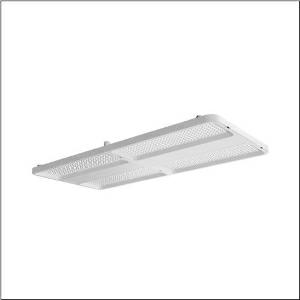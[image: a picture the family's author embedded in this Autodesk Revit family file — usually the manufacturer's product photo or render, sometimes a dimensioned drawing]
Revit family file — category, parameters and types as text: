
# Revit family: highbay_21_maxi_52hn12db4qda
name_source: partatom
category: Lighting Fixtures
units: mm (PartAtom-declared; Revit-internal decimal feet)

## family parameters
Cut with Voids When Loaded = No
Host = Face
Light Source = No
Part Type = Normal
Room Calculation Point = No
Round Connector Dimension = Use Diameter
Shared = No

## types (1)
- --- (1 x LED, 5840 lm, 31.4 W, 4000K)
    Apparent Load = 31 VA
    CIE Flux Codes = 90 98 100 100 100
    Color Rendering = 80
    Color Temperature = 4000K
    Default Elevation = 1800 mm
    Description = high bay luminaire Highbay 21 maxi; direct symmetric wide distribution, light control with lens of PMMA; UGR ≤ 22 (X = 4H | Y = 8H | S = 0.25H | reflection values 70/50/20); luminous flux: 38.000lm; light colour: 840, colour temperature: 4000K, MacAdam ≤ 3 SDCM (initial), colour rendering: CRI > 80; luminous efficacy: 192,2lm/W; rated service life: 75.000h (L80) at AT= ta max; control: DALI 2; luminaire connection: terminal, 5-pole, max. 2.5mm² (cable entry for one cable, Ø 8.5..16mm); mains connection: 230..240V, AC/DC 0/50..60Hz; connected load: 197,7W; protection rating (complete): IP66; insulation class (complete): insulation class I (protective earthing); protection symbol: D; impact resistance: IK08; certification: CE, ENEC, VDE, UKCA; luminaire for central battery installations according to EN 60598-2-22, internal wiring halogen-free; luminaire LABS conformity tested according to VDMA 24364:2018-05; Suitable for use in the food industry according to the specifications of IFS-Food, HACCP and/or BRC; housing frame of high-performance plastic PA6, matt traffic white (RAL 9016); cover of PMMA; dimension (LxWxH): 946 x 442 x 72mm; permissible operating ambient temperature: -40..+60°C (reducing of maximum allowable ambient temperature of 5°C with ceiling mounting); packaging unit: 1 piece; (delivery without accessories; please order mounting accessories separately)
    Height = 72 mm  [stored 0.23622 ft]
    Lamp = 1 x LED
    Lamp Light Flux = 5840 lm
    Lamp Power = 31.4 W
    Lamp count = 1
    Length = 946 mm
    Luminous efficacy = 186 lm/W
    Manufacturer = Siteco
    ModVariant = No
    Model = 52HN12DB4QDA
    Mounting Place = Ceiling
    Mounting Type = Pendant
    Number of Poles = 1
    OnlyDefault = Yes
    Power Factor = 1
    Product Name = Highbay 21 maxi
    Product group = high bay luminaire
    ProductGroupID = 902
    Protection Class = Protection class I
    Protection Degree = IP 66
    RLX_Detail_Level = 1
    RLX_Emergency_Light_Flux = 0 lm
    RLX_Emergency_Type = 0
    RLX_Emergency_Type_DB = No
    RlxData = <blob elided: 128149 chars, md5=0320493b>
    Socket = socket
    Standby Power = 0 W
    System Light Flux = 5840 lm
    System Power = 31 W
    Type Comments = : DC mode (central or group accumulator) initial emergency light level
    Type Image = l_1363244.jpg
    URL = http://relux.com
    VarID = @adj_017717
    Voltage = 0 V
    Weight = 0.00 kg
    Width = 442 mm

note: [stored X ft] marks values corroborated as IEEE doubles in the binary element streams (Revit-internal decimal feet)

## geometry (parser evidence)
native form markers: Blend x4, Sweep x9
no freeform markers — native parametric forms only
